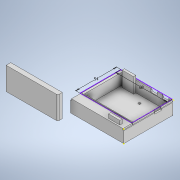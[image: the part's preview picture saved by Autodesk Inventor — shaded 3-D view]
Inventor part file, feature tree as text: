
AUTODESK INVENTOR PART (.ipt)
format: ipt  version: 2022 (Build 260153000, 153)  size: 270,848 bytes
history: native  units: in
note: dims shown in document units (in); Inventor stores cm internally (conversion verified against a paired STEP export)
features: extrude x9, sketch x8, fillet x4, hole x1, thread x1
ambient origin geometry x8: Origin, YZ Plane, XZ Plane, XY Plane, X Axis, Y Axis, Z Axis, Center Point
bodies: Solid1 (feature_tree)
feature tree (23):
  sketch  "Sketch1"  dims[d0=2.7559in d2=0.6594in d3=0.0in]
  extrude  "Extrusion1"  Depth=0.6594in TaperAngle=0.0deg
  extrude  "Extrusion2"  Depth=0.0787in
  extrude  "Extrusion3"  Depth=0.0787in
  extrude  "Extrusion4"  Depth=0.0787in TaperAngle=0.0deg
  extrude  "Extrusion5"  Depth=0.0787in TaperAngle=0.0deg
  extrude  "Extrusion6"  Depth=0.1181in
  extrude  "Extrusion7"  Depth=0.7874in TaperAngle=0.0deg
  hole  "Hole1"  [1 undecoded]
  extrude  "Extrusion8"  Depth=0.0394in
  extrude  "Extrusion9"  Depth=0.1181in
  thread  "Thread1"  [1 undecoded]
  fillet  "Fillet7"  Radius=1.1811in
  fillet  "Fillet8"  Radius=0.9161in
  fillet  "Fillet9"  Radius=0.8465in
  fillet  "Fillet10"  Radius=0.2756in
  sketch  "Sketch4"  dims[d5=0.0787in d6=0.0787in]
  sketch  "Sketch7"  dims[d7=0.0787in d11=0.0787in]
  sketch  "Sketch10"  dims[d13=0.5807in d14=0.0in d44=0.0787in d45=0.0in]
  sketch  "Sketch11"  dims[d46=2.6772in d48=0.0787in d49=0.0in]
  sketch  "Sketch13"  dims[d57=0.5906in d58=0.1181in]
  sketch  "Sketch14"  dims[d61=0.5906in d64=0.7874in d65=0.0in]
  sketch  "Sketch15"  dims[d72=0.3543in d73=0.0in d75=0.0787in d76=0.0394in d79=0.1181in d81=0.2362in d82=1.1811in d83=0.0in d85=0.9161in d86=0.8465in d88=0.2756in d89=0.1181in d91=0.25in d92=0.25in d93=0.2362in d94=0.1575in d95=0.0787in d96=90.0deg d97=0.2362in d98=0.0in d99=0.3346in d100=0.3346in d101=0.1575in d103=0.5315in d104=1.126in d105=0.0709in d106=0.3937in d107=0.0in d108=0.3543in d109=0.1969in d111=0.9843in d113=0.0591in d114=0.3937in d115=0.0in d116=0.2362in d117=0.0in d119=0.4528in d120=0.3937in d121=0.0787in d122=0.0787in d123=0.0787in d124=0.0787in d132=1.9685in d133=2.5197in d135=2.6772in d136=2.126in d138=2.5984in d139=0.0394in d140=0.0394in d141=0.0394in d143=2.6772in d144=0.4724in d40=0.0197in d41=0.0344in d42=0.0197in d43=0.0344in d66=0.0197in d67=0.0344in d84=0.0197in]
note: 2 required parameter values undecoded (feature->parameter linkage not recoverable at this tier; creation-order binding heuristic only, values carry confidence <= 0.55)
